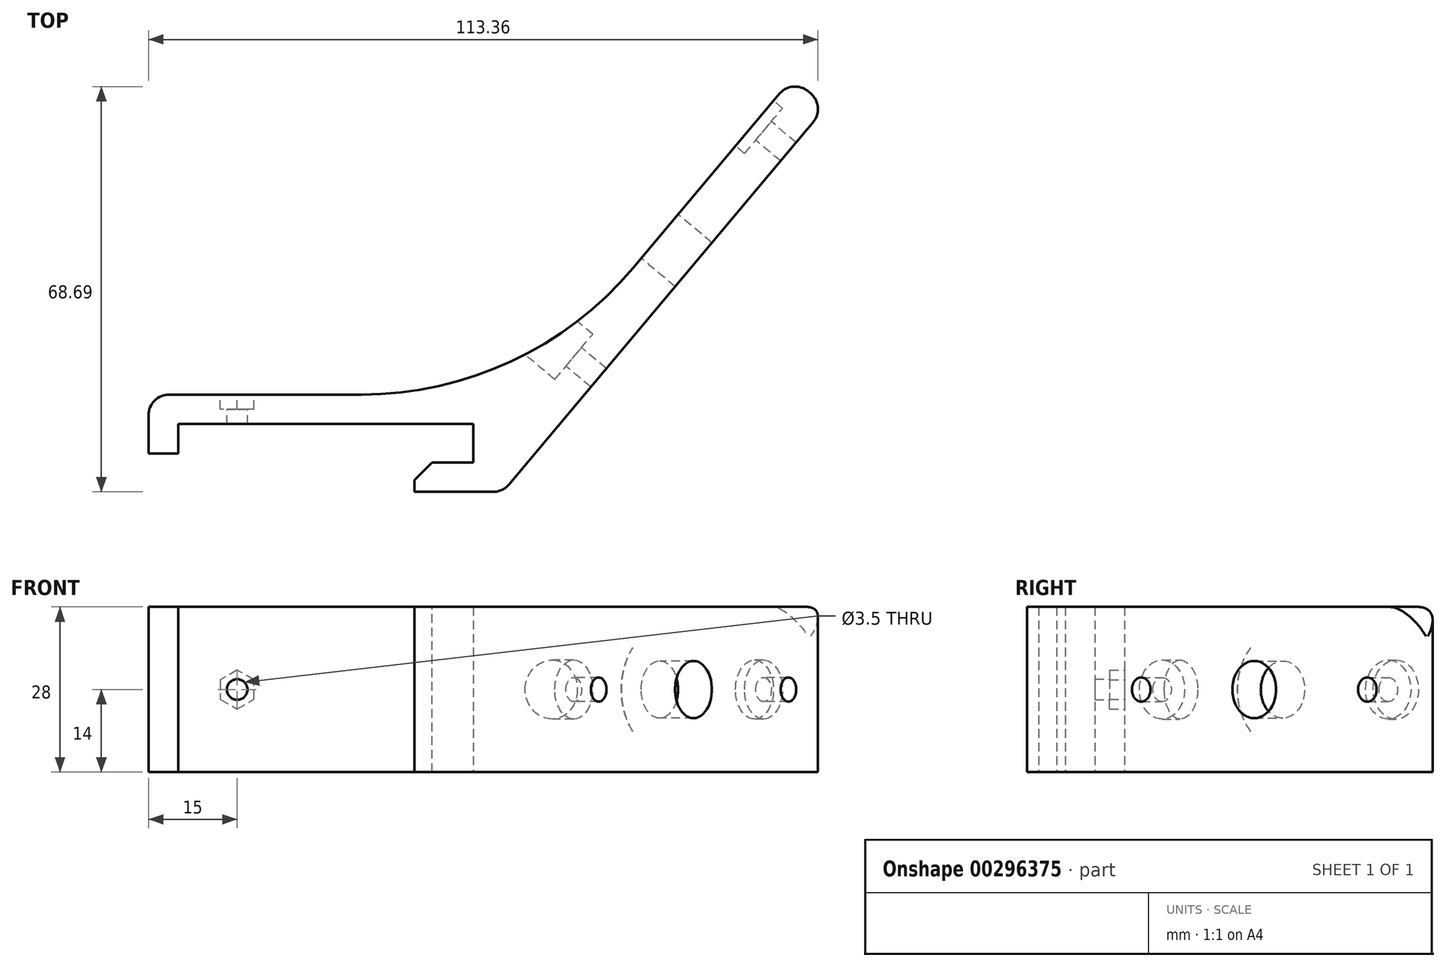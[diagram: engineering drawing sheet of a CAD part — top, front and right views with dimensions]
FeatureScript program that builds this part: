
annotation { "Feature Type Name" : "Feature", "Feature Type Description" : "" }
export const myFeature = defineFeature(function(context is Context, id is Id, definition is map)
    precondition{}
    {
        {
            var Q0;
            Q0=qCreatedBy(makeId("Top.planeOp"),FACE);
            var sketch = newSketch(context, id + "F0", { "sketchPlane" : qUnion([Q0])});
            skLineSegment(sketch, "E0", {"start": v(0, 0) * mm, "end": v(0, 10) * mm});
            skLineSegment(sketch, "E1", {"start": v(0, 10) * mm, "end": v(64.05, 10) * mm});
            skLineSegment(sketch, "E2", {"start": v(60, -6.5) * mm, "end": v(45, -6.5) * mm});
            skLineSegment(sketch, "E3", {"start": v(45, -6.5) * mm, "end": v(45, -1.5) * mm});
            skLineSegment(sketch, "E4", {"start": v(45, -1.5) * mm, "end": v(55, -1.5) * mm});
            skLineSegment(sketch, "E5", {"start": v(55, -1.5) * mm, "end": v(55, 5) * mm});
            skLineSegment(sketch, "E6", {"start": v(55, 5) * mm, "end": v(5, 5) * mm});
            skLineSegment(sketch, "E7", {"start": v(5, 5) * mm, "end": v(5, 0) * mm});
            skLineSegment(sketch, "E8", {"start": v(5, 0) * mm, "end": v(0, 0) * mm});
            skLineSegment(sketch, "E9", {"start": v(60, -6.5) * mm, "end": v(114.8, 58.8) * mm});
            skLineSegment(sketch, "E10", {"start": v(114.8, 58.8) * mm, "end": v(109.05, 63.62) * mm});
            skLineSegment(sketch, "E11", {"start": v(109.05, 63.62) * mm, "end": v(64.05, 10) * mm});
            skSolve(sketch);
        }
        {
            var Q0;
            Q0=qSketchRegion(id+"F0",true);
            extrude(context, id + "F1", {"entities" : qUnion([Q0]), "depth" : 28 * mm});
        }
        {
            var Q0;
            Q0=makeQuery(id+"F1.opExtrude","SWEPT_FACE",FACE,{"disambiguationData":[OSD([sQuery(id+"F0.wireOp",EDGE,"E1")])]});
            var sketch = newSketch(context, id + "F2", { "sketchPlane" : qUnion([Q0])});
            skCircle(sketch, "E12", {"center": v(-15, 14) * mm, "radius": 1.75 * mm});
            skPoint(sketch, "E12.centerSnap0", {"position": v(0, 14) * mm});
            skSolve(sketch);
        }
        {
            var Q0;
            Q0=qSketchRegion(id+"F2",true);
            extrude(context, id + "F3", {"entities" : qUnion([Q0]), "operationType" : NewBodyOperationType.REMOVE, "endBound" : BoundingType.THROUGH_ALL, "oppositeDirection" : true, "depth" : 25 * mm});
        }
        {
            var Q0;
            Q0=makeQuery(id+"F1.opExtrude","SWEPT_FACE",FACE,{"disambiguationData":[OSD([sQuery(id+"F0.wireOp",EDGE,"E1")])]});
            var sketch = newSketch(context, id + "F4", { "sketchPlane" : qUnion([Q0])});
            skCircle(sketch, "E13.cCircle", {"center": v(-15, 14) * mm, "radius": 2.85 * mm, "construction": true});
            skLineSegment(sketch, "E13.0", {"start": v(-12.15, 15.65) * mm, "end": v(-12.15, 12.35) * mm});
            skLineSegment(sketch, "E13.1", {"start": v(-12.15, 12.35) * mm, "end": v(-15, 10.7) * mm});
            skLineSegment(sketch, "E13.2", {"start": v(-15, 10.7) * mm, "end": v(-17.85, 12.35) * mm});
            skLineSegment(sketch, "E13.3", {"start": v(-17.85, 12.35) * mm, "end": v(-17.85, 15.65) * mm});
            skLineSegment(sketch, "E13.4", {"start": v(-17.85, 15.65) * mm, "end": v(-15, 17.3) * mm});
            skLineSegment(sketch, "E13.5", {"start": v(-15, 17.3) * mm, "end": v(-12.15, 15.65) * mm});
            skPoint(sketch, "E13.0.midPoint", {"position": v(-12.15, 14) * mm});
            skSolve(sketch);
        }
        {
            var Q0;
            Q0=qSketchRegion(id+"F4",true);
            extrude(context, id + "F5", {"entities" : qUnion([Q0]), "operationType" : NewBodyOperationType.REMOVE, "oppositeDirection" : true, "depth" : 2.5 * mm});
        }
        {
            var Q0;
            Q0=makeQuery(id+"F1.opExtrude","SWEPT_FACE",FACE,{"disambiguationData":[OSD([sQuery(id+"F0.wireOp",EDGE,"E11")])]});
            var sketch = newSketch(context, id + "F6", { "sketchPlane" : qUnion([Q0])});
            skCircle(sketch, "E14", {"center": v(-108.83, 14) * mm, "radius": 2.05 * mm});
            skPoint(sketch, "E14.centerSnap0", {"position": v(-118.83, 14) * mm});
            skCircle(sketch, "E15", {"center": v(-58.83, 14) * mm, "radius": 2.05 * mm});
            skCircle(sketch, "E16", {"center": v(-83.83, 14) * mm, "radius": 4.85 * mm});
            skSolve(sketch);
        }
        {
            var Q0;
            Q0 = qSketchRegion(id + "F6", true);
            extrude(context, id + "F7", {"entities" : qUnion([Q0]), "operationType" : NewBodyOperationType.REMOVE, "endBound" : BoundingType.THROUGH_ALL, "oppositeDirection" : true, "depth" : 25 * mm});
        }
        {
            var Q0;
            Q0=makeQuery(id+"F1.opExtrude","CAP_FACE",FACE,{"disambiguationData":[OSD([sQuery(id+"F0.wireOp",EDGE,"E0"),sQuery(id+"F0.wireOp",EDGE,"E1"),sQuery(id+"F0.wireOp",EDGE,"E2"),sQuery(id+"F0.wireOp",EDGE,"E3"),sQuery(id+"F0.wireOp",EDGE,"E4"),sQuery(id+"F0.wireOp",EDGE,"E5"),sQuery(id+"F0.wireOp",EDGE,"E6"),sQuery(id+"F0.wireOp",EDGE,"E7"),sQuery(id+"F0.wireOp",EDGE,"E8"),sQuery(id+"F0.wireOp",EDGE,"E9"),sQuery(id+"F0.wireOp",EDGE,"E10"),sQuery(id+"F0.wireOp",EDGE,"E11")])],"isStart":true});
            var sketch = newSketch(context, id + "F8", { "sketchPlane" : qUnion([Q0])});
            skLineSegment(sketch, "E17.0", {"start": v(32.03, -10) * mm, "end": v(64.05, -10) * mm});
            skLineSegment(sketch, "E18.0", {"start": v(86.55, -36.81) * mm, "end": v(64.05, -10) * mm});
            skLineSegment(sketch, "E19", {"start": v(86.55, -36.81) * mm, "end": v(32.03, -10) * mm});
            skPoint(sketch, "E20.orphan", {"position": v(109.05, -63.62) * mm});
            skPoint(sketch, "E21.orphan", {"position": v(0, -10) * mm});
            skSolve(sketch);
        }
        {
            var Q0;
            Q0=makeQuery(id+"F1.opExtrude","CAP_FACE",FACE,{"disambiguationData":[OSD([sQuery(id+"F0.wireOp",EDGE,"E0"),sQuery(id+"F0.wireOp",EDGE,"E1"),sQuery(id+"F0.wireOp",EDGE,"E2"),sQuery(id+"F0.wireOp",EDGE,"E3"),sQuery(id+"F0.wireOp",EDGE,"E4"),sQuery(id+"F0.wireOp",EDGE,"E5"),sQuery(id+"F0.wireOp",EDGE,"E6"),sQuery(id+"F0.wireOp",EDGE,"E7"),sQuery(id+"F0.wireOp",EDGE,"E8"),sQuery(id+"F0.wireOp",EDGE,"E9"),sQuery(id+"F0.wireOp",EDGE,"E10"),sQuery(id+"F0.wireOp",EDGE,"E11")])],"isStart":false});
            var sketch = newSketch(context, id + "F9", { "sketchPlane" : qUnion([Q0])});
            skLineSegment(sketch, "E22.0.0", {"start": v(32.03, 10) * mm, "end": v(86.55, 36.81) * mm});
            skLineSegment(sketch, "E22.0.1", {"start": v(86.55, 36.81) * mm, "end": v(64.05, 10) * mm});
            skLineSegment(sketch, "E22.0.2", {"start": v(64.05, 10) * mm, "end": v(32.03, 10) * mm});
            skSolve(sketch);
        }
        {
            var Q0;
            Q0=makeQuery(id+"F1.opExtrude","SWEPT_FACE",FACE,{"disambiguationData":[OSD([sQuery(id+"F0.wireOp",EDGE,"E11")])]});
            var sketch = newSketch(context, id + "F10", { "sketchPlane" : qUnion([Q0])});
            skCircle(sketch, "E23", {"center": v(-58.83, 14) * mm, "radius": 5 * mm});
            skCircle(sketch, "E24", {"center": v(-108.83, 14) * mm, "radius": 5 * mm});
            skSolve(sketch);
        }
        {
            var Q0;
            Q0 = qSketchRegion(id + "F10", true);
            extrude(context, id + "F11", {"entities" : qUnion([Q0]), "operationType" : NewBodyOperationType.REMOVE, "oppositeDirection" : true, "depth" : 2 * mm});
        }
        {
            var Q0;
            Q0=makeQuery(id+"F1.opExtrude","SWEPT_EDGE",EDGE,{"disambiguationData":[OSD([sQuery(id+"F0.wireOp",EDGE,"E1"),sQuery(id+"F0.wireOp",EDGE,"E11")])]});
            var Q1;
            Q1=makeQuery(id+"F648N01kTSayZlW_1.opExtrude","SWEPT_EDGE",EDGE,{"disambiguationData":[OSD([sQuery(id+"F0.wireOp",EDGE,"E1"),sQuery(id+"F8.wireOp",EDGE,"E17.0"),sQuery(id+"F8.wireOp",EDGE,"E19")])]});
            var Q2;
            Q2=makeQuery(id+"FnIAIQcXoPNKTlm_1.opExtrude","SWEPT_EDGE",EDGE,{"disambiguationData":[OSD([sQuery(id+"F0.wireOp",EDGE,"E1"),sQuery(id+"F9.wireOp",EDGE,"E22.0.0"),sQuery(id+"F9.wireOp",EDGE,"E22.0.2")])]});
            var Q3;
            Q3=makeQuery(id+"F648N01kTSayZlW_1.opExtrude","SWEPT_EDGE",EDGE,{"disambiguationData":[OSD([sQuery(id+"F0.wireOp",EDGE,"E11"),sQuery(id+"F8.wireOp",EDGE,"E18.0"),sQuery(id+"F8.wireOp",EDGE,"E19")])]});
            var Q4;
            Q4=makeQuery(id+"FnIAIQcXoPNKTlm_1.opExtrude","SWEPT_EDGE",EDGE,{"disambiguationData":[OSD([sQuery(id+"F0.wireOp",EDGE,"E11"),sQuery(id+"F9.wireOp",EDGE,"E22.0.0"),sQuery(id+"F9.wireOp",EDGE,"E22.0.1")])]});
            fillet(context, id + "F12", {"entities" : qUnion([Q0, Q1, Q2, Q3, Q4]), "radius" : 60 * mm, "tangentPropagation" : true, "allowEdgeOverflow" : false});
        }
        {
            var Q0;
            Q0=makeQuery(id+"F1.opExtrude","SWEPT_EDGE",EDGE,{"disambiguationData":[OSD([sQuery(id+"F0.wireOp",EDGE,"E0"),sQuery(id+"F0.wireOp",EDGE,"E1")])]});
            var Q1;
            Q1=makeQuery(id+"F1.opExtrude","SWEPT_EDGE",EDGE,{"disambiguationData":[OSD([sQuery(id+"F0.wireOp",EDGE,"E10"),sQuery(id+"F0.wireOp",EDGE,"E11")])]});
            var Q2;
            Q2=makeQuery(id+"F1.opExtrude","SWEPT_EDGE",EDGE,{"disambiguationData":[OSD([sQuery(id+"F0.wireOp",EDGE,"E9"),sQuery(id+"F0.wireOp",EDGE,"E10")])]});
            var Q3;
            Q3=makeQuery(id+"F1.opExtrude","SWEPT_EDGE",EDGE,{"disambiguationData":[OSD([sQuery(id+"F0.wireOp",EDGE,"E2"),sQuery(id+"F0.wireOp",EDGE,"E9")])]});
            fillet(context, id + "F13", {"entities" : qUnion([Q0, Q1, Q2, Q3]), "radius" : 3.5 * mm, "tangentPropagation" : true, "allowEdgeOverflow" : false});
        }
        {
            var Q0;
            Q0=makeQuery(id+"F1.opExtrude","SWEPT_EDGE",EDGE,{"disambiguationData":[OSD([sQuery(id+"F0.wireOp",EDGE,"E3"),sQuery(id+"F0.wireOp",EDGE,"E4")])]});
            chamfer(context, id + "F14", {"entities" : qUnion([Q0]), "width" : 3 * mm, "tangentPropagation" : true});
        }
        {
            var Q0;
            Q0=makeQuery(id+"F1.opExtrude","SWEPT_FACE",FACE,{"disambiguationData":[OSD([sQuery(id+"F0.wireOp",EDGE,"E11")])]});
            var sketch = newSketch(context, id + "F15", { "sketchPlane" : qUnion([Q0])});
            skCircle(sketch, "E25", {"center": v(-83.83, 14) * mm, "radius": 10 * mm});
            skSolve(sketch);
        }
        {
            var Q0;
            Q0 = qSketchRegion(id + "F15", true);
            extrude(context, id + "F16", {"entities" : qUnion([Q0]), "operationType" : NewBodyOperationType.REMOVE, "endBound" : BoundingType.THROUGH_ALL, "depth" : 25 * mm});
        }
        {
            var Q0;
            Q0=makeQuery(id+"F1.opExtrude","SWEPT_FACE",FACE,{"disambiguationData":[OSD([sQuery(id+"F0.wireOp",EDGE,"E9")])]});
            var sketch = newSketch(context, id + "F17", { "sketchPlane" : qUnion([Q0])});
            skLineSegment(sketch, "E26.0.0", {"start": v(39.18, 28) * mm, "end": v(34.2, 28) * mm, "construction": true});
            skLineSegment(sketch, "E26.0.1", {"start": v(34.2, 28) * mm, "end": v(27.78, 28) * mm, "construction": true});
            skLineSegment(sketch, "E26.0.2", {"start": v(27.78, 28) * mm, "end": v(23.95, 28) * mm, "construction": true});
            skLineSegment(sketch, "E26.0.3", {"start": v(23.95, 28) * mm, "end": v(33.59, 28) * mm, "construction": true});
            skLineSegment(sketch, "E26.0.4", {"start": v(33.59, 28) * mm, "end": v(118.83, 28) * mm, "construction": true});
            skLineSegment(sketch, "E26.0.6", {"start": v(118.83, 28) * mm, "end": v(83.83, 28) * mm, "construction": true});
            skLineSegment(sketch, "E26.0.7", {"start": v(83.83, 28) * mm, "end": v(48.83, 28) * mm, "construction": true});
            skLineSegment(sketch, "E26.0.8", {"start": v(48.83, 28) * mm, "end": v(28.25, 28) * mm, "construction": true});
            skLineSegment(sketch, "E26.0.9", {"start": v(28.25, 28) * mm, "end": v(7.66, 28) * mm, "construction": true});
            skLineSegment(sketch, "E26.0.10", {"start": v(7.66, 28) * mm, "end": v(0, 28) * mm, "construction": true});
            skLineSegment(sketch, "E26.0.11", {"start": v(0, 28) * mm, "end": v(3.21, 28) * mm, "construction": true});
            skLineSegment(sketch, "E26.0.12", {"start": v(3.21, 28) * mm, "end": v(7.04, 28) * mm, "construction": true});
            skLineSegment(sketch, "E26.0.13", {"start": v(7.04, 28) * mm, "end": v(39.18, 28) * mm, "construction": true});
            skLineSegment(sketch, "E27.0", {"start": v(118.83, 0) * mm, "end": v(118.83, 28) * mm, "construction": true});
            skArc(sketch, "E28", {"start": v(118.83, 23) * mm, "mid": v(117.37, 26.54) * mm, "end": v(113.83, 28) * mm});
            skLineSegment(sketch, "E29", {"start": v(113.83, 28) * mm, "end": v(118.83, 28) * mm});
            skLineSegment(sketch, "E30", {"start": v(118.83, 23) * mm, "end": v(118.83, 28) * mm});
            skSolve(sketch);
        }
        {
            var Q0;
            Q0 = qSketchRegion(id + "F17", true);
            extrude(context, id + "F18", {"entities" : qUnion([Q0]), "operationType" : NewBodyOperationType.REMOVE, "endBound" : BoundingType.THROUGH_ALL, "oppositeDirection" : true, "depth" : 25 * mm});
        }
    });
